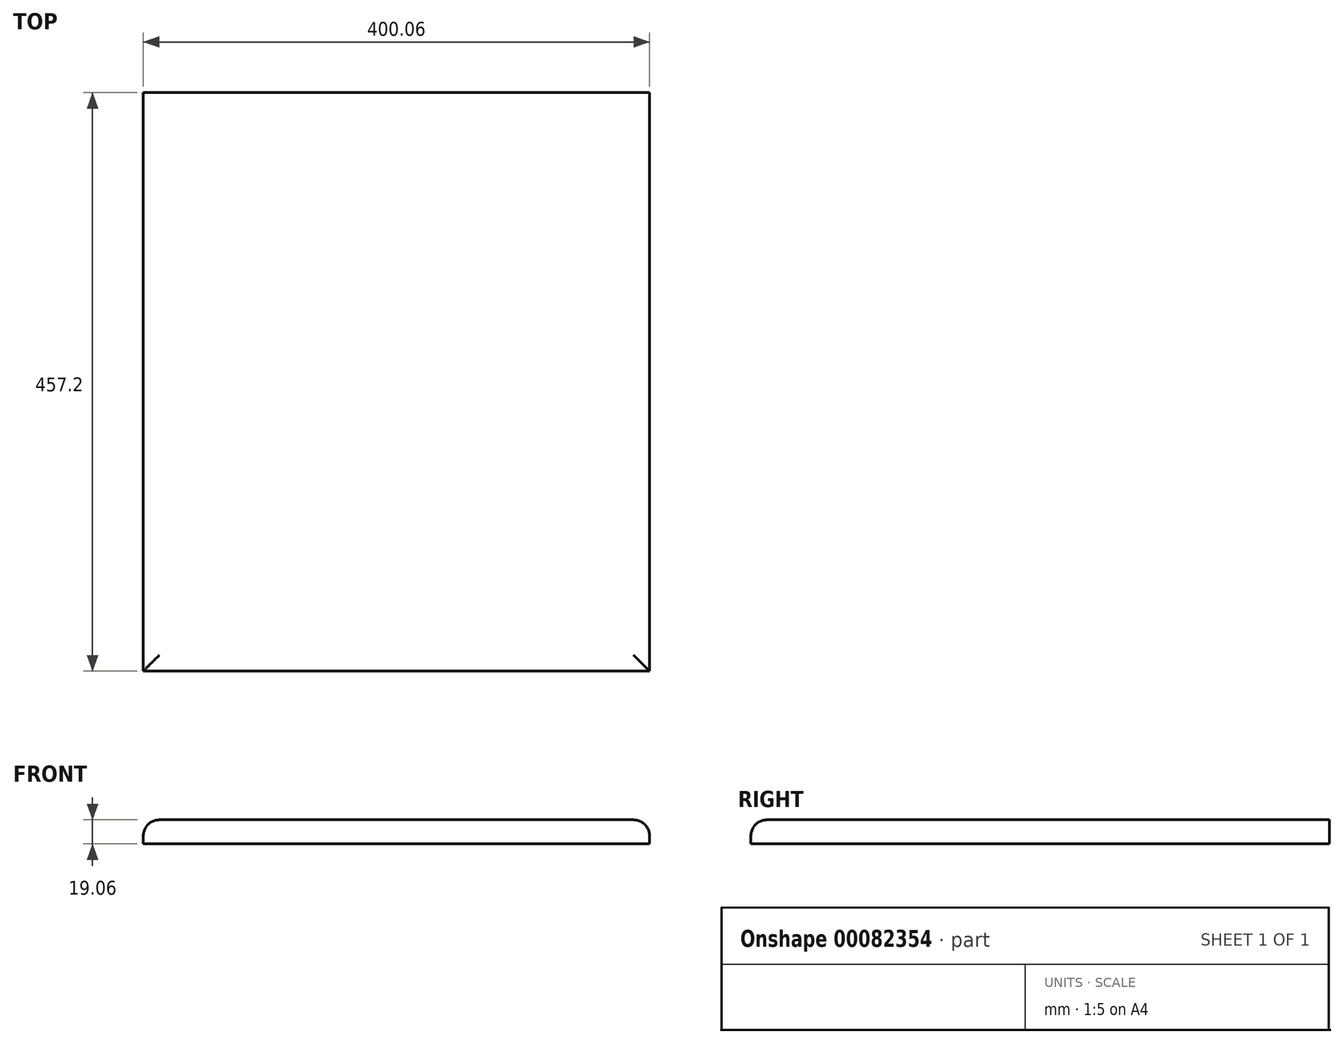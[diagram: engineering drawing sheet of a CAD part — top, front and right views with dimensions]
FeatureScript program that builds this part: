
annotation { "Feature Type Name" : "Feature", "Feature Type Description" : "" }
export const myFeature = defineFeature(function(context is Context, id is Id, definition is map)
    precondition{}
    {
        {
            var Q0;
            Q0=qCreatedBy(makeId("Front.planeOp"),FACE);
            var sketch = newSketch(context, id + "F0", { "sketchPlane" : qUnion([Q0])});
            skLineSegment(sketch, "E0.bottom", {"start": v(200.03, 9.53) * mm, "end": v(-200.03, 9.53) * mm});
            skLineSegment(sketch, "E0.top", {"start": v(200.03, -9.53) * mm, "end": v(-200.03, -9.53) * mm});
            skLineSegment(sketch, "E0.left", {"start": v(200.03, 9.53) * mm, "end": v(200.03, -9.53) * mm});
            skLineSegment(sketch, "E0.right", {"start": v(-200.03, 9.53) * mm, "end": v(-200.03, -9.53) * mm});
            skPoint(sketch, "E0.middle", {"position": v(0, 0) * mm});
            skSolve(sketch);
        }
        {
            var Q0;
            Q0 = qSketchRegion(id + "F0", true);
            extrude(context, id + "F1", {"entities" : qUnion([Q0]), "depth" : 457.2 * mm, "symmetric" : true});
        }
        {
            var Q0;
            Q0=makeQuery(id+"F1.opExtrude","SWEPT_EDGE",EDGE,{"disambiguationData":[OSD([sQuery(id+"F0.wireOp",EDGE,"E0.bottom"),sQuery(id+"F0.wireOp",EDGE,"E0.right")])]});
            var Q1;
            Q1=makeQuery(id+"F1.opExtrude","CAP_EDGE",EDGE,{"disambiguationData":[OSD([sQuery(id+"F0.wireOp",EDGE,"E0.bottom")])],"isStart":false});
            var Q2;
            Q2=makeQuery(id+"F1.opExtrude","SWEPT_EDGE",EDGE,{"disambiguationData":[OSD([sQuery(id+"F0.wireOp",EDGE,"E0.bottom"),sQuery(id+"F0.wireOp",EDGE,"E0.left")])]});
            fillet(context, id + "F2", {"entities" : qUnion([Q0, Q1, Q2]), "radius" : 12.7 * mm, "tangentPropagation" : true, "allowEdgeOverflow" : false});
        }
    });
